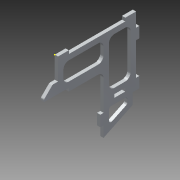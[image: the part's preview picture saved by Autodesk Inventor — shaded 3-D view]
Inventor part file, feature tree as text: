
AUTODESK INVENTOR PART (.ipt)
format: ipt  version: 2013 (Build 170138000, 138)  size: 211,456 bytes
history: native  units: mm
features: sketch x2, extrude x1
ambient origin geometry x8: Origin, YZ Plane, XZ Plane, XY Plane, X Axis, Y Axis, Z Axis, Center Point
feature tree (3):
  sketch  "Sketch1"  dims[d4=10.0mm d5=52.0mm]
  extrude  "Extrusion5"  Depth=52.0mm
  sketch  "Sketch2"  dims[d6=10.0mm d8=10.0mm d11=3.0mm d15=3.0mm d29=10.0mm d33=5.0mm d36=5.0mm d40=5.0mm d46=30.0mm d47=3.0mm d48=10.0mm d50=3.0mm d53=42.0mm d55=10.0mm d57=3.0mm d59=5.0mm d60=5.0mm d61=5.0mm d62=10.0mm d63=3.0mm d64=10.0mm d67=53.0mm d68=27.0mm d69=5.0mm d75=90.0deg d76=90.0deg d77=90.0deg d78=3.0mm d79=90.0deg d80=6.0mm d81=30.000027mm d82=27.0mm d83=10.0mm d84=10.0mm d85=3.0mm d86=3.0mm d87=30.0mm d90=5.0mm d91=13.0mm d92=33.0mm d95=2.0mm d97=5.0mm d98=5.0mm d99=5.0mm d100=5.0mm d101=2.0mm d102=3.0mm d103=0.0mm d104=5.0mm d105=5.0mm d106=8.0mm d107=33.0mm d108=23.0mm d109=3.0mm d110=2.0mm d111=10.0mm]
